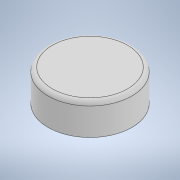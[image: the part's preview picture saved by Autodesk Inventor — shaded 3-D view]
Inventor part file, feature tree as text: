
AUTODESK INVENTOR PART (.ipt)
format: ipt  version: 2022 (Build 260153000, 153)  size: 115,712 bytes
history: native  units: mm
features: extrude x2, sketch x1, fillet x1, chamfer x1
ambient origin geometry x8: Origin, YZ Plane, XZ Plane, XY Plane, X Axis, Y Axis, Z Axis, Center Point
bodies: Solid1 (feature_tree)
feature tree (5):
  sketch  "Sketch1"  dims[d0=0.2mm d1=7.5mm d2=0.0mm d3=1.0mm d4=2.0mm d5=0.0mm d6=0.5mm d7=2.0mm d8=45.0deg]
  extrude  "Extrusion1"  Depth=7.5mm TaperAngle=0.0deg
  fillet  "Fillet1"  Radius=1.0mm
  extrude  "Extrusion2"  Depth=2.0mm TaperAngle=0.0deg
  chamfer  "Chamfer1"  Distance=2.0mm Angle=45.0deg
